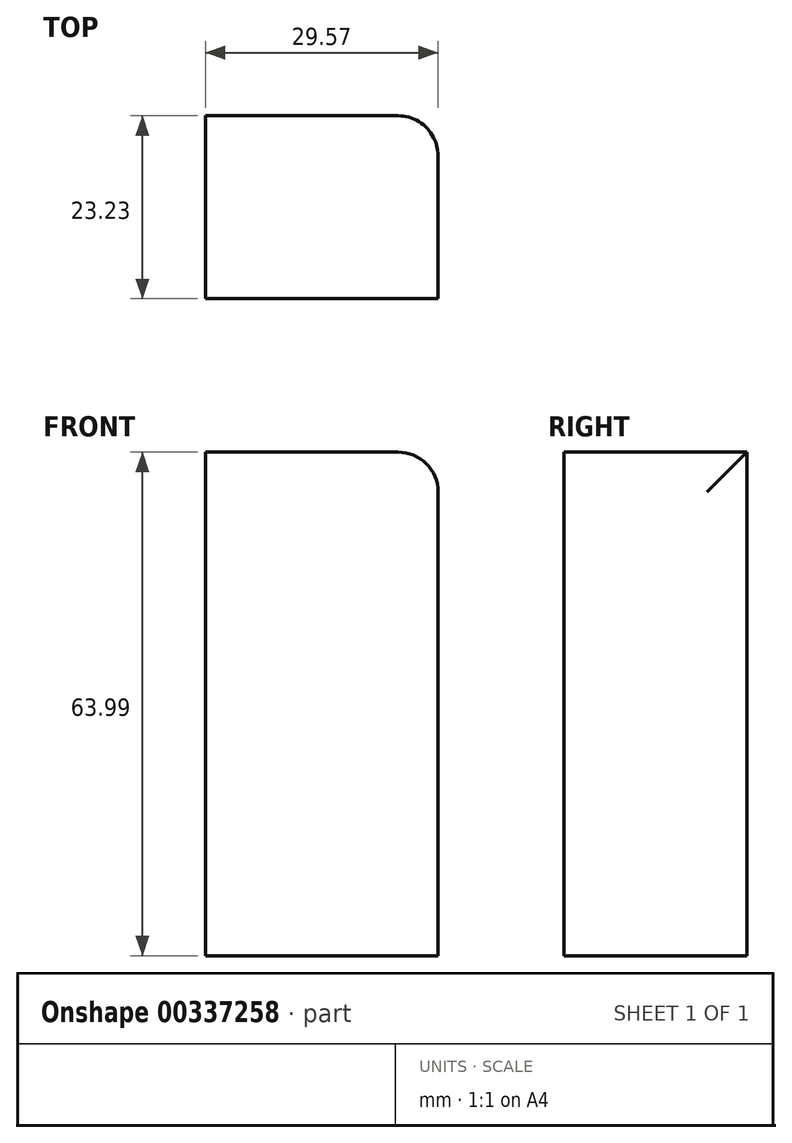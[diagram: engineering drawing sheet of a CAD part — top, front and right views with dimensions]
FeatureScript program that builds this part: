
annotation { "Feature Type Name" : "Feature", "Feature Type Description" : "" }
export const myFeature = defineFeature(function(context is Context, id is Id, definition is map)
    precondition{}
    {
        {
            var Q0;
            Q0=qCreatedBy(makeId("Top.planeOp"),FACE);
            var sketch = newSketch(context, id + "F0", { "sketchPlane" : qUnion([Q0])});
            skLineSegment(sketch, "E0.bottom", {"start": v(19.9, 23.23) * mm, "end": v(49.47, 23.23) * mm});
            skLineSegment(sketch, "E0.top", {"start": v(19.9, 0) * mm, "end": v(49.47, 0) * mm});
            skLineSegment(sketch, "E0.left", {"start": v(19.9, 23.23) * mm, "end": v(19.9, 0) * mm});
            skLineSegment(sketch, "E0.right", {"start": v(49.47, 23.23) * mm, "end": v(49.47, 0) * mm});
            skLineSegment(sketch, "E1.bottom", {"start": v(49.47, 0) * mm, "end": v(49.47, 0) * mm});
            skLineSegment(sketch, "E1.top", {"start": v(49.47, 23.23) * mm, "end": v(49.47, 23.23) * mm});
            skLineSegment(sketch, "E1.left", {"start": v(49.47, 0) * mm, "end": v(49.47, 23.23) * mm, "construction": true});
            skLineSegment(sketch, "E1.right", {"start": v(49.47, 0) * mm, "end": v(49.47, 23.23) * mm, "construction": true});
            skSolve(sketch);
        }
        {
            var Q0;
            Q0=makeQuery(id+"F0.imprint","IMPRINT",FACE,{"disambiguationData":[TD([[makeQuery(id+"F0.imprint","IMPRINT",EDGE,{"derivedFrom":sQuery(id+"F0.wireOp",EDGE,"E0.bottom")}),-1.0]])]});
            extrude(context, id + "F1", {"entities" : qUnion([Q0]), "oppositeDirection" : true, "depth" : 64 * mm});
        }
        {
            var Q0;
            Q0=makeQuery(id+"F1.opExtrude","SWEPT_EDGE",EDGE,{"disambiguationData":[OSD([sQuery(id+"F0.wireOp",EDGE,"E0.bottom"),sQuery(id+"F0.wireOp",EDGE,"E0.right")])]});
            var Q1;
            Q1=makeQuery(id+"F1.opExtrude","CAP_EDGE",EDGE,{"disambiguationData":[OSD([sQuery(id+"F0.wireOp",EDGE,"E0.right")])],"isStart":true});
            fillet(context, id + "F2", {"entities" : qUnion([Q0, Q1]), "radius" : 5.08 * mm, "tangentPropagation" : true, "allowEdgeOverflow" : false});
        }
        {
            var Q0;
            Q0=makeQuery(id+"F1.opExtrude","SWEPT_FACE",FACE,{"disambiguationData":[OSD([sQuery(id+"F0.wireOp",EDGE,"E0.top")])]});
            var sketch = newSketch(context, id + "F3", { "sketchPlane" : qUnion([Q0])});
            skSolve(sketch);
        }
    });
